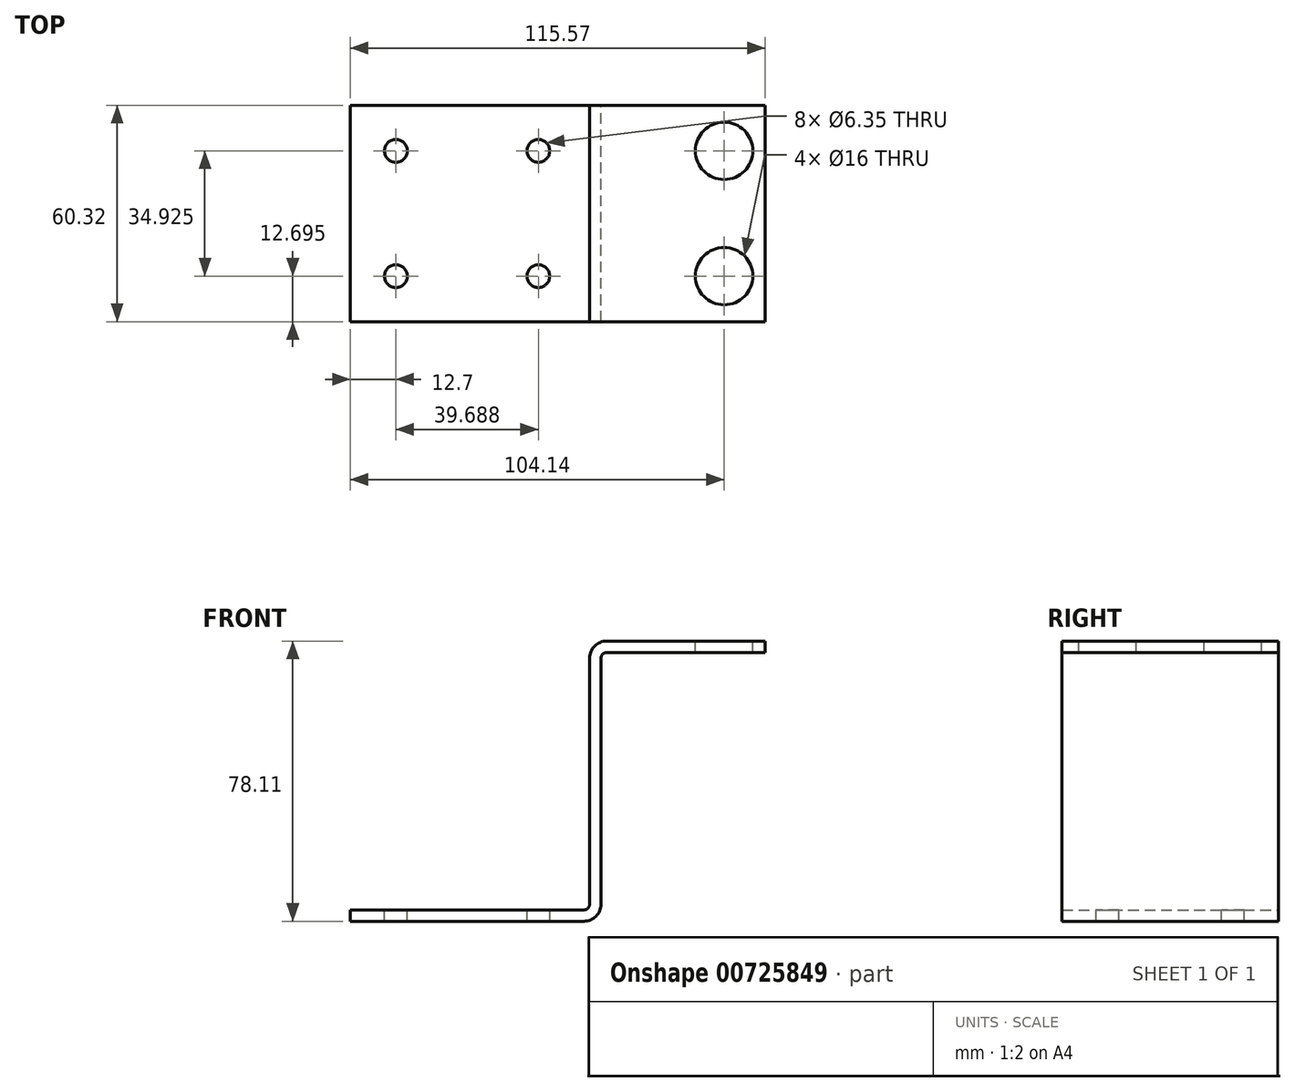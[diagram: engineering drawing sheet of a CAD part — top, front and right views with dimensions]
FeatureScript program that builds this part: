
annotation { "Feature Type Name" : "Feature", "Feature Type Description" : "" }
export const myFeature = defineFeature(function(context is Context, id is Id, definition is map)
    precondition{}
    {
        {
            var Q0;
            Q0=qCreatedBy(makeId("Front.planeOp"),FACE);
            var sketch = newSketch(context, id + "F0", { "sketchPlane" : qUnion([Q0])});
            skLineSegment(sketch, "E0.bottom", {"start": v(-69.85, 3.18) * mm, "end": v(-4.76, 3.18) * mm});
            skLineSegment(sketch, "E0.top", {"start": v(-69.85, 0) * mm, "end": v(-4.76, 0) * mm});
            skLineSegment(sketch, "E0.left", {"start": v(-69.85, 3.18) * mm, "end": v(-69.85, 0) * mm});
            skLineSegment(sketch, "E0.right", {"start": v(0, 0) * mm, "end": v(0, 0) * mm});
            skLineSegment(sketch, "E1.left", {"start": v(0, 4.76) * mm, "end": v(0, 73.34) * mm});
            skLineSegment(sketch, "E2.left", {"start": v(-3.18, 78.1) * mm, "end": v(-3.18, 78.1) * mm});
            skLineSegment(sketch, "E2.right", {"start": v(45.72, 78.1) * mm, "end": v(45.72, 74.93) * mm});
            skLineSegment(sketch, "E3", {"start": v(-3.18, 4.76) * mm, "end": v(-3.18, 73.34) * mm});
            skLineSegment(sketch, "E4", {"start": v(1.59, 74.93) * mm, "end": v(45.72, 74.93) * mm});
            skLineSegment(sketch, "E5", {"start": v(1.59, 78.1) * mm, "end": v(45.72, 78.1) * mm});
            skPoint(sketch, "E6.visualSharp", {"position": v(0, 74.93) * mm});
            skArc(sketch, "E6.filletArc", {"start": v(1.59, 74.93) * mm, "mid": v(0.46, 74.47) * mm, "end": v(0, 73.34) * mm});
            skPoint(sketch, "E7.visualSharp", {"position": v(-3.18, 78.1) * mm});
            skArc(sketch, "E7.filletArc", {"start": v(1.59, 78.1) * mm, "mid": v(-1.78, 76.71) * mm, "end": v(-3.18, 73.34) * mm});
            skPoint(sketch, "E8.visualSharp", {"position": v(-3.18, 3.18) * mm});
            skArc(sketch, "E8.filletArc", {"start": v(-4.76, 3.18) * mm, "mid": v(-3.64, 3.64) * mm, "end": v(-3.18, 4.76) * mm});
            skPoint(sketch, "E9.visualSharp", {"position": v(0, 0) * mm});
            skArc(sketch, "E9.filletArc", {"start": v(-4.76, 0) * mm, "mid": v(-1.4, 1.4) * mm, "end": v(0, 4.76) * mm});
            skSolve(sketch);
        }
        {
            var Q0;
            Q0=makeQuery(id+"F0.imprint","IMPRINT",FACE,{"disambiguationData":[TD([[makeQuery(id+"F0.imprint","IMPRINT",EDGE,{"derivedFrom":sQuery(id+"F0.wireOp",EDGE,"E0.bottom")}),-1.0]])]});
            extrude(context, id + "F1", {"entities" : qUnion([Q0]), "depth" : 60.32 * mm, "offsetDistance" : 25.4 * mm});
        }
        {
            var Q0;
            Q0=makeQuery(id+"F1.opExtrude","SWEPT_FACE",FACE,{"disambiguationData":[OSD([sQuery(id+"F0.wireOp",EDGE,"E5")])]});
            var sketch = newSketch(context, id + "F2", { "sketchPlane" : qUnion([Q0])});
            skCircle(sketch, "E10", {"center": v(34.29, -12.7) * mm, "radius": 8 * mm});
            skCircle(sketch, "E11", {"center": v(34.29, -47.63) * mm, "radius": 8 * mm});
            skSolve(sketch);
        }
        {
            var Q0;
            Q0 = qSketchRegion(id + "F2", true);
            extrude(context, id + "F3", {"entities" : qUnion([Q0]), "operationType" : NewBodyOperationType.REMOVE, "oppositeDirection" : true, "depth" : 25.4 * mm, "offsetDistance" : 25.4 * mm});
        }
        {
            var Q0;
            Q0=makeQuery(id+"F1.opExtrude","SWEPT_FACE",FACE,{"disambiguationData":[OSD([sQuery(id+"F0.wireOp",EDGE,"E0.bottom")])]});
            var sketch = newSketch(context, id + "F4", { "sketchPlane" : qUnion([Q0])});
            skCircle(sketch, "E12", {"center": v(-17.46, -12.7) * mm, "radius": 3.18 * mm});
            skCircle(sketch, "E13", {"center": v(-17.46, -47.62) * mm, "radius": 3.18 * mm});
            skCircle(sketch, "E14", {"center": v(-57.15, -12.7) * mm, "radius": 3.18 * mm});
            skCircle(sketch, "E15", {"center": v(-57.15, -47.62) * mm, "radius": 3.18 * mm});
            skSolve(sketch);
        }
        {
            var Q0;
            Q0=makeQuery(id+"F4.imprint","IMPRINT",FACE,{"disambiguationData":[TD([[makeQuery(id+"F4.imprint","IMPRINT",EDGE,{"derivedFrom":sQuery(id+"F4.wireOp",EDGE,"E14")}),1.0]])]});
            var Q1;
            Q1=makeQuery(id+"F4.imprint","IMPRINT",FACE,{"disambiguationData":[TD([[makeQuery(id+"F4.imprint","IMPRINT",EDGE,{"derivedFrom":sQuery(id+"F4.wireOp",EDGE,"E12")}),1.0]])]});
            var Q2;
            Q2=makeQuery(id+"F4.imprint","IMPRINT",FACE,{"disambiguationData":[TD([[makeQuery(id+"F4.imprint","IMPRINT",EDGE,{"derivedFrom":sQuery(id+"F4.wireOp",EDGE,"E13")}),1.0]])]});
            var Q3;
            Q3=makeQuery(id+"F4.imprint","IMPRINT",FACE,{"disambiguationData":[TD([[makeQuery(id+"F4.imprint","IMPRINT",EDGE,{"derivedFrom":sQuery(id+"F4.wireOp",EDGE,"E15")}),1.0]])]});
            var Q4;
            Q4=sQuery(id+"F4.wireOp",EDGE,"E14");
            var Q5;
            Q5=sQuery(id+"F4.wireOp",EDGE,"E12");
            var Q6;
            Q6=sQuery(id+"F4.wireOp",EDGE,"E13");
            var Q7;
            Q7=sQuery(id+"F4.wireOp",EDGE,"E15");
            extrude(context, id + "F5", {"entities" : qUnion([Q0, Q1, Q2, Q3]), "operationType" : NewBodyOperationType.REMOVE, "surfaceEntities" : qUnion([Q4, Q5, Q6, Q7]), "oppositeDirection" : true, "depth" : 25.4 * mm, "offsetDistance" : 25.4 * mm});
        }
    });
